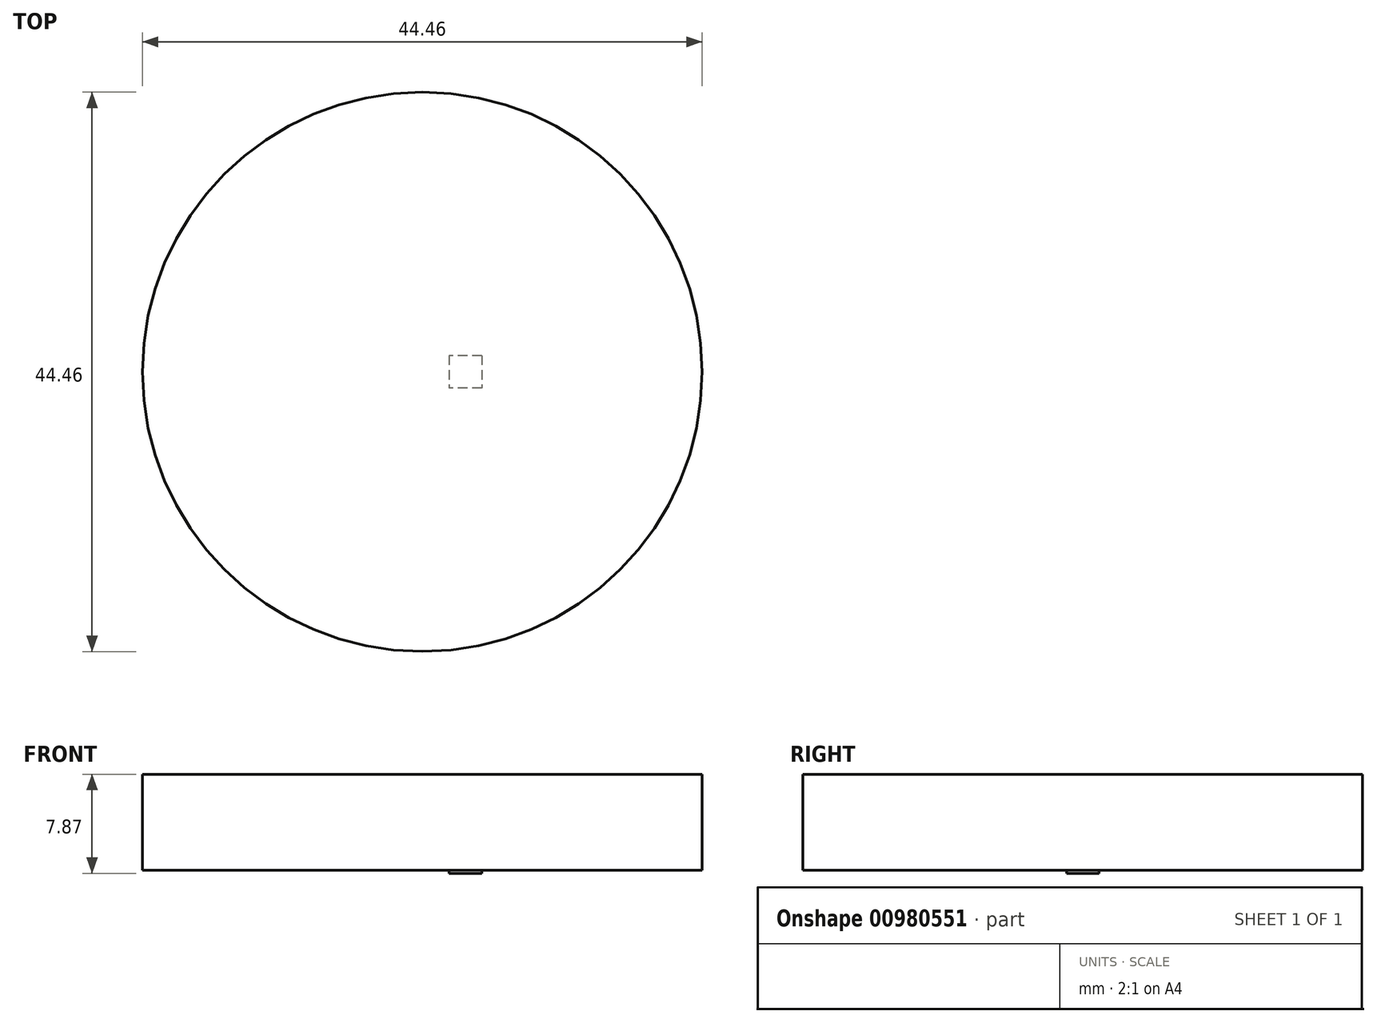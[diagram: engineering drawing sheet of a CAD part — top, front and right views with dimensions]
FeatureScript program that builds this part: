
annotation { "Feature Type Name" : "Feature", "Feature Type Description" : "" }
export const myFeature = defineFeature(function(context is Context, id is Id, definition is map)
    precondition{}
    {
        {
            var Q0;
            Q0=qCreatedBy(makeId("Top.planeOp"),FACE);
            var sketch = newSketch(context, id + "F0", { "sketchPlane" : qUnion([Q0])});
            skCircle(sketch, "E0", {"center": v(0, 0) * mm, "radius": 22.23 * mm});
            skSolve(sketch);
        }
        {
            var Q0;
            Q0=makeQuery(id+"F0.imprint","IMPRINT",FACE,{"disambiguationData":[TD([[makeQuery(id+"F0.imprint","IMPRINT",EDGE,{"derivedFrom":sQuery(id+"F0.wireOp",EDGE,"E0")}),1.0]])]});
            extrude(context, id + "F1", {"entities" : qUnion([Q0]), "depth" : 7.62 * mm, "offsetDistance" : 25.4 * mm});
        }
        {
            var Q0;
            Q0=makeQuery(id+"F1.opExtrude","CAP_FACE",FACE,{"disambiguationData":[OSD([sQuery(id+"F0.wireOp",EDGE,"E0")])],"isStart":true});
            var sketch = newSketch(context, id + "F2", { "sketchPlane" : qUnion([Q0])});
            skLineSegment(sketch, "E1.bottom", {"start": v(4.73, -1.3) * mm, "end": v(2.12, -1.3) * mm});
            skLineSegment(sketch, "E1.top", {"start": v(4.73, 1.3) * mm, "end": v(2.12, 1.3) * mm});
            skLineSegment(sketch, "E1.left", {"start": v(4.73, -1.3) * mm, "end": v(4.73, 1.3) * mm});
            skLineSegment(sketch, "E1.right", {"start": v(2.12, -1.3) * mm, "end": v(2.12, 1.3) * mm});
            skPoint(sketch, "E1.middle", {"position": v(3.42, 0) * mm});
            skSolve(sketch);
        }
        {
            var Q0;
            Q0 = qSketchRegion(id + "F2", true);
            extrude(context, id + "F3", {"entities" : qUnion([Q0]), "operationType" : NewBodyOperationType.ADD, "depth" : 0.25 * mm, "offsetDistance" : 25.4 * mm});
        }
    });
